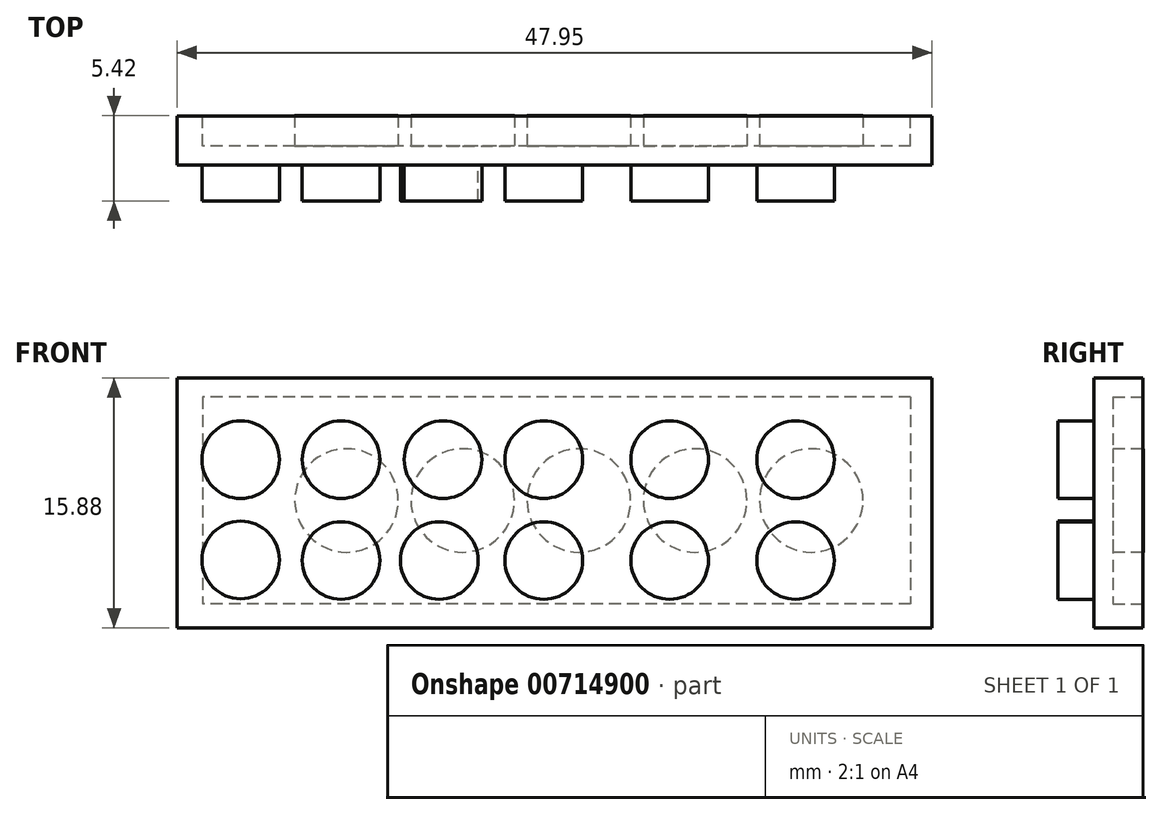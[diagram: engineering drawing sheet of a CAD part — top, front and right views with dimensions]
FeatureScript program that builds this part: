
annotation { "Feature Type Name" : "Feature", "Feature Type Description" : "" }
export const myFeature = defineFeature(function(context is Context, id is Id, definition is map)
    precondition{}
    {
        {
            var Q0;
            Q0=qCreatedBy(makeId("Front.planeOp"),FACE);
            var sketch = newSketch(context, id + "F0", { "sketchPlane" : qUnion([Q0])});
            skLineSegment(sketch, "E0.bottom", {"start": v(-86.74, 45.15) * mm, "end": v(-38.8, 45.15) * mm});
            skLineSegment(sketch, "E0.top", {"start": v(-86.74, 29.27) * mm, "end": v(-38.8, 29.27) * mm});
            skLineSegment(sketch, "E0.left", {"start": v(-86.74, 45.15) * mm, "end": v(-86.74, 29.27) * mm});
            skLineSegment(sketch, "E0.right", {"start": v(-38.8, 45.15) * mm, "end": v(-38.8, 29.27) * mm});
            skCircle(sketch, "E1", {"center": v(-83.5, 41.64) * mm, "radius": 2.46 * mm});
            skCircle(sketch, "E2", {"center": v(-83.5, 34.2) * mm, "radius": 2.46 * mm});
            skCircle(sketch, "E3", {"center": v(-76.45, 41.64) * mm, "radius": 2.46 * mm});
            skCircle(sketch, "E4", {"center": v(-76.45, 34.2) * mm, "radius": 2.46 * mm});
            skCircle(sketch, "E5", {"center": v(-69.29, 41.64) * mm, "radius": 2.46 * mm});
            skCircle(sketch, "E6", {"center": v(-69.29, 34.2) * mm, "radius": 2.46 * mm});
            skCircle(sketch, "E7", {"center": v(0, 0) * mm, "radius": 2.2 * mm});
            skCircle(sketch, "E8.1.0.0", {"center": v(-44.29, 41.64) * mm, "radius": 2.46 * mm});
            skCircle(sketch, "E8.1.0.2", {"center": v(-44.29, 34.2) * mm, "radius": 2.46 * mm});
            skCircle(sketch, "E8.2.0.0", {"center": v(-19.29, 41.64) * mm, "radius": 2.46 * mm});
            skCircle(sketch, "E8.2.0.2", {"center": v(-19.29, 34.2) * mm, "radius": 2.46 * mm});
            skCircle(sketch, "E9", {"center": v(-62.2, 41.64) * mm, "radius": 2.46 * mm});
            skCircle(sketch, "E10", {"center": v(-53.68, 41.64) * mm, "radius": 2.46 * mm});
            skCircle(sketch, "E11", {"center": v(-61.76, 34.2) * mm, "radius": 2.46 * mm});
            skCircle(sketch, "E12", {"center": v(-53.8, 34.2) * mm, "radius": 2.46 * mm});
            skSolve(sketch);
        }
        {
            var Q0;
            Q0=makeQuery(id+"F0.imprint","IMPRINT",FACE,{"disambiguationData":[TD([[makeQuery(id+"F0.imprint","IMPRINT",EDGE,{"derivedFrom":sQuery(id+"F0.wireOp",EDGE,"E0.bottom")}),-1.0]])]});
            var Q1;
            Q1=makeQuery(id+"F0.imprint","IMPRINT",FACE,{"disambiguationData":[TD([[makeQuery(id+"F0.imprint","IMPRINT",EDGE,{"derivedFrom":sQuery(id+"F0.wireOp",EDGE,"E1")}),1.0]])]});
            var Q2;
            Q2=makeQuery(id+"F0.imprint","IMPRINT",FACE,{"disambiguationData":[TD([[makeQuery(id+"F0.imprint","IMPRINT",EDGE,{"derivedFrom":sQuery(id+"F0.wireOp",EDGE,"E2")}),1.0]])]});
            var Q3;
            Q3=makeQuery(id+"F0.imprint","IMPRINT",FACE,{"disambiguationData":[TD([[makeQuery(id+"F0.imprint","IMPRINT",EDGE,{"derivedFrom":sQuery(id+"F0.wireOp",EDGE,"E4")}),1.0]])]});
            var Q4;
            Q4=makeQuery(id+"F0.imprint","IMPRINT",FACE,{"disambiguationData":[TD([[makeQuery(id+"F0.imprint","IMPRINT",EDGE,{"derivedFrom":sQuery(id+"F0.wireOp",EDGE,"E3")}),1.0]])]});
            var Q5;
            Q5=makeQuery(id+"F0.imprint","IMPRINT",FACE,{"disambiguationData":[TD([[makeQuery(id+"F0.imprint","IMPRINT",EDGE,{"derivedFrom":sQuery(id+"F0.wireOp",EDGE,"E6")}),1.0]])]});
            var Q6;
            Q6=makeQuery(id+"F0.imprint","IMPRINT",FACE,{"disambiguationData":[TD([[makeQuery(id+"F0.imprint","IMPRINT",EDGE,{"derivedFrom":sQuery(id+"F0.wireOp",EDGE,"E5")}),1.0]])]});
            var Q7;
            Q7=makeQuery(id+"F0.imprint","IMPRINT",FACE,{"disambiguationData":[TD([[makeQuery(id+"F0.imprint","IMPRINT",EDGE,{"derivedFrom":sQuery(id+"F0.wireOp",EDGE,"E11")}),1.0]])]});
            var Q8;
            Q8=makeQuery(id+"F0.imprint","IMPRINT",FACE,{"disambiguationData":[TD([[makeQuery(id+"F0.imprint","IMPRINT",EDGE,{"derivedFrom":sQuery(id+"F0.wireOp",EDGE,"E9")}),1.0]])]});
            var Q9;
            Q9=makeQuery(id+"F0.imprint","IMPRINT",FACE,{"disambiguationData":[TD([[makeQuery(id+"F0.imprint","IMPRINT",EDGE,{"derivedFrom":sQuery(id+"F0.wireOp",EDGE,"E12")}),1.0]])]});
            var Q10;
            Q10=makeQuery(id+"F0.imprint","IMPRINT",FACE,{"disambiguationData":[TD([[makeQuery(id+"F0.imprint","IMPRINT",EDGE,{"derivedFrom":sQuery(id+"F0.wireOp",EDGE,"E10")}),1.0]])]});
            var Q11;
            Q11=makeQuery(id+"F0.imprint","IMPRINT",FACE,{"disambiguationData":[TD([[makeQuery(id+"F0.imprint","IMPRINT",EDGE,{"derivedFrom":sQuery(id+"F0.wireOp",EDGE,"E8.1.0.2")}),1.0]])]});
            var Q12;
            Q12=makeQuery(id+"F0.imprint","IMPRINT",FACE,{"disambiguationData":[TD([[makeQuery(id+"F0.imprint","IMPRINT",EDGE,{"derivedFrom":sQuery(id+"F0.wireOp",EDGE,"E8.1.0.0")}),1.0]])]});
            extrude(context, id + "F1", {"entities" : qUnion([Q0, Q1, Q2, Q3, Q4, Q5, Q6, Q7, Q8, Q9, Q10, Q11, Q12]), "depth" : 3.12 * mm, "offsetDistance" : 25 * mm});
        }
        {
            var Q0;
            Q0=makeQuery(id+"F1.opExtrude","CAP_FACE",FACE,{"disambiguationData":[OSD([sQuery(id+"F0.wireOp",EDGE,"E0.bottom"),sQuery(id+"F0.wireOp",EDGE,"E0.top"),sQuery(id+"F0.wireOp",EDGE,"E0.left"),sQuery(id+"F0.wireOp",EDGE,"E0.right")])],"isStart":false});
            var sketch = newSketch(context, id + "F2", { "sketchPlane" : qUnion([Q0])});
            skSolve(sketch);
        }
        {
            var Q0;
            Q0=makeQuery(id+"F2.imprint","IMPRINT",FACE,{"disambiguationData":[TD([[makeQuery(id+"F2.imprint","IMPRINT",EDGE,{"derivedFrom":makeQuery(id+"F1.opExtrude","CAP_EDGE",EDGE,{"disambiguationData":[OSD([sQuery(id+"F0.wireOp",EDGE,"E0.bottom")])],"isStart":false})}),-1.0]])]});
            var sketch = newSketch(context, id + "F3", { "sketchPlane" : qUnion([Q0])});
            skLineSegment(sketch, "E13", {"start": v(-86.43, 39.95) * mm, "end": v(-84.12, 39.95) * mm});
            skCircle(sketch, "E14", {"center": v(-82.7, 39.96) * mm, "radius": 2.46 * mm});
            skCircle(sketch, "E15", {"center": v(-82.7, 33.59) * mm, "radius": 2.46 * mm});
            skCircle(sketch, "E16", {"center": v(-76.32, 39.96) * mm, "radius": 2.46 * mm});
            skCircle(sketch, "E17", {"center": v(-76.32, 33.55) * mm, "radius": 2.46 * mm});
            skCircle(sketch, "E18", {"center": v(-69.84, 39.96) * mm, "radius": 2.46 * mm});
            skCircle(sketch, "E19", {"center": v(-63.44, 39.96) * mm, "radius": 2.46 * mm});
            skCircle(sketch, "E20", {"center": v(-55.45, 39.96) * mm, "radius": 2.46 * mm});
            skCircle(sketch, "E21", {"center": v(-70.08, 33.55) * mm, "radius": 2.46 * mm});
            skCircle(sketch, "E22", {"center": v(-63.44, 33.55) * mm, "radius": 2.46 * mm});
            skCircle(sketch, "E23", {"center": v(-55.45, 33.55) * mm, "radius": 2.46 * mm});
            skCircle(sketch, "E24", {"center": v(-47.45, 33.55) * mm, "radius": 2.46 * mm});
            skCircle(sketch, "E25", {"center": v(-47.45, 39.96) * mm, "radius": 2.46 * mm});
            skSolve(sketch);
        }
        {
            var Q0;
            Q0 = qSketchRegion(id + "F3", true);
            extrude(context, id + "F4", {"entities" : qUnion([Q0]), "operationType" : NewBodyOperationType.ADD, "depth" : 2.28 * mm, "offsetDistance" : 25 * mm});
        }
        {
            var Q0;
            Q0=makeQuery(id+"F1.opExtrude","CAP_FACE",FACE,{"disambiguationData":[OSD([sQuery(id+"F0.wireOp",EDGE,"E0.bottom"),sQuery(id+"F0.wireOp",EDGE,"E0.top"),sQuery(id+"F0.wireOp",EDGE,"E0.left"),sQuery(id+"F0.wireOp",EDGE,"E0.right")])],"isStart":true});
            var sketch = newSketch(context, id + "F5", { "sketchPlane" : qUnion([Q0])});
            skLineSegment(sketch, "E26.bottom", {"start": v(40.14, 43.94) * mm, "end": v(85.13, 43.94) * mm});
            skLineSegment(sketch, "E26.top", {"start": v(40.14, 30.8) * mm, "end": v(85.13, 30.8) * mm});
            skLineSegment(sketch, "E26.left", {"start": v(40.14, 43.94) * mm, "end": v(40.14, 30.8) * mm});
            skLineSegment(sketch, "E26.right", {"start": v(85.13, 43.94) * mm, "end": v(85.13, 30.8) * mm});
            skSolve(sketch);
        }
        {
            var Q0;
            Q0 = qSketchRegion(id + "F5", true);
            extrude(context, id + "F6", {"entities" : qUnion([Q0]), "operationType" : NewBodyOperationType.REMOVE, "oppositeDirection" : true, "depth" : 1.91 * mm, "offsetDistance" : 25 * mm});
        }
        {
            var Q0;
            Q0=makeQuery(id+"F6.boolean.opBoolean","COPY",FACE,{"derivedFrom":makeQuery(id+"F6.opExtrude","CAP_FACE",FACE,{"disambiguationData":[OSD([sQuery(id+"F5.wireOp",EDGE,"E26.bottom"),sQuery(id+"F5.wireOp",EDGE,"E26.top"),sQuery(id+"F5.wireOp",EDGE,"E26.left"),sQuery(id+"F5.wireOp",EDGE,"E26.right")])],"isStart":false})});
            var sketch = newSketch(context, id + "F7", { "sketchPlane" : qUnion([Q0])});
            skCircle(sketch, "E27", {"center": v(46.45, 37.37) * mm, "radius": 3.29 * mm});
            skCircle(sketch, "E28", {"center": v(53.83, 37.37) * mm, "radius": 3.29 * mm});
            skCircle(sketch, "E29", {"center": v(61.21, 37.37) * mm, "radius": 3.29 * mm});
            skCircle(sketch, "E30", {"center": v(68.6, 37.37) * mm, "radius": 3.29 * mm});
            skLineSegment(sketch, "E31", {"start": v(68.6, 37.37) * mm, "end": v(71.88, 37.37) * mm});
            skCircle(sketch, "E32", {"center": v(75.97, 37.37) * mm, "radius": 3.29 * mm});
            skPoint(sketch, "E33.start.orphan", {"position": v(40.14, 37.37) * mm});
            skSolve(sketch);
        }
        {
            var Q0;
            Q0 = qSketchRegion(id + "F7", true);
            extrude(context, id + "F8", {"entities" : qUnion([Q0]), "operationType" : NewBodyOperationType.ADD, "depth" : 1.93 * mm, "offsetDistance" : 25 * mm});
        }
    });
